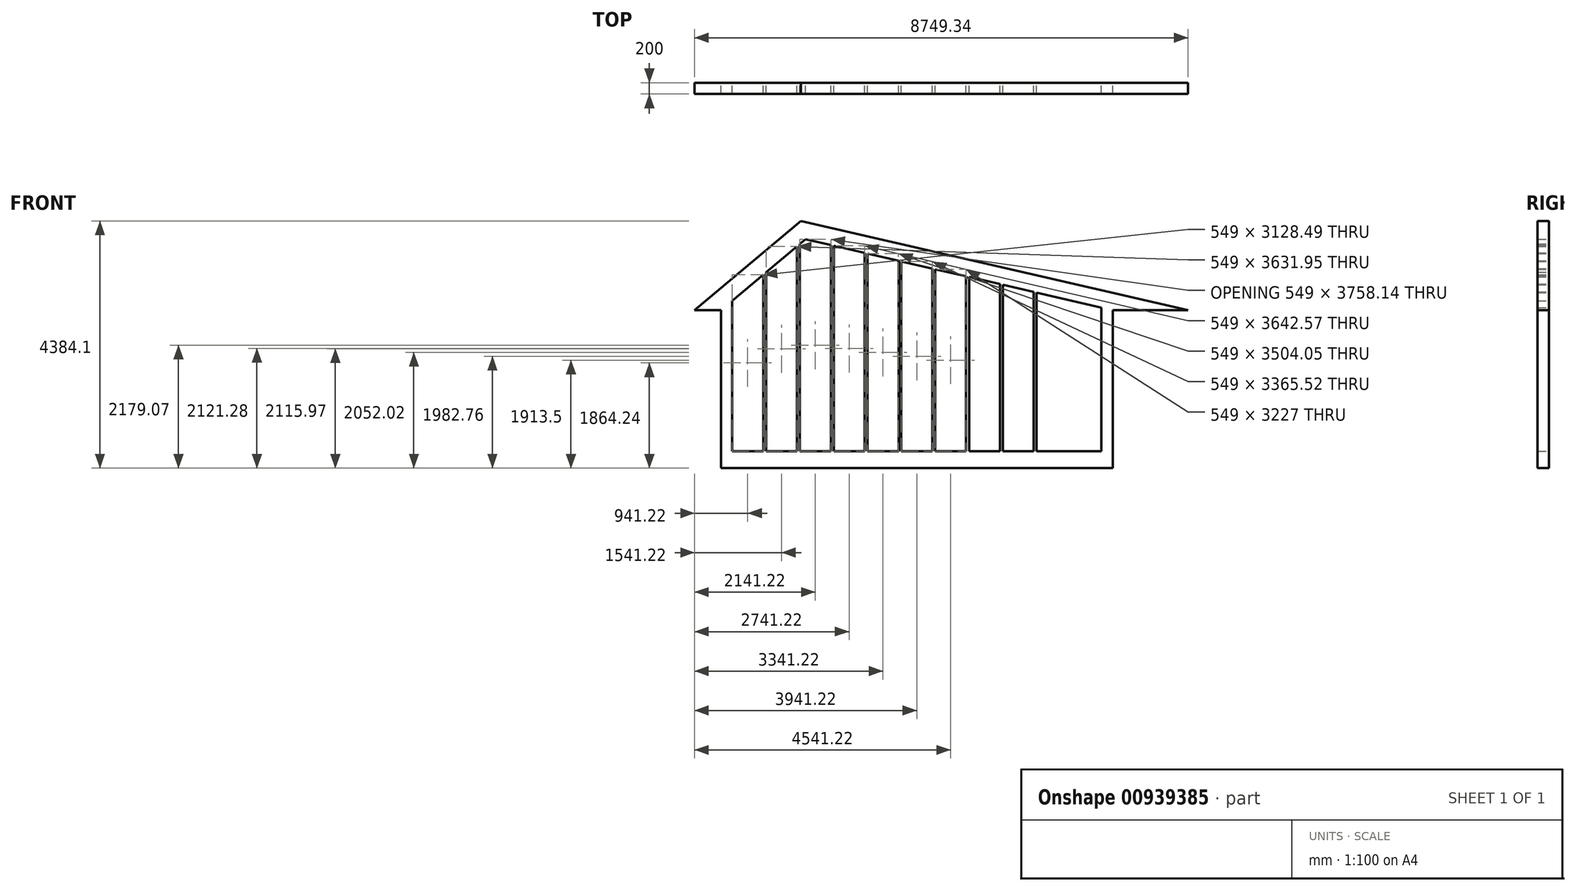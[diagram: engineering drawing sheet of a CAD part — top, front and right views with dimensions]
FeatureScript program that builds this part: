
annotation { "Feature Type Name" : "Feature", "Feature Type Description" : "" }
export const myFeature = defineFeature(function(context is Context, id is Id, definition is map)
    precondition{}
    {
        {
            var Q0;
            Q0=qCreatedBy(makeId("Front.planeOp"),FACE);
            var sketch = newSketch(context, id + "F0", { "sketchPlane" : qUnion([Q0])});
            skLineSegment(sketch, "E0", {"start": v(0, 0) * mm, "end": v(0, 2667.82) * mm});
            skLineSegment(sketch, "E1", {"start": v(0, 2667.82) * mm, "end": v(1299.4, 3758.14) * mm});
            skLineSegment(sketch, "E2", {"start": v(1299.4, 3758.14) * mm, "end": v(6549, 2546.17) * mm});
            skLineSegment(sketch, "E3", {"start": v(6549, 2546.17) * mm, "end": v(6549, 0) * mm});
            skLineSegment(sketch, "E4", {"start": v(6549, 0) * mm, "end": v(0, 0) * mm});
            skLineSegment(sketch, "E5", {"start": v(-200, -300) * mm, "end": v(-200, 2500) * mm});
            skLineSegment(sketch, "E6", {"start": v(-200, 2500) * mm, "end": v(-666.72, 2500) * mm});
            skLineSegment(sketch, "E7", {"start": v(-666.72, 2500) * mm, "end": v(1221.14, 4084.1) * mm});
            skLineSegment(sketch, "E8", {"start": v(1221.14, 4084.1) * mm, "end": v(8082.62, 2500) * mm});
            skLineSegment(sketch, "E9", {"start": v(8082.62, 2500) * mm, "end": v(6749, 2500) * mm});
            skLineSegment(sketch, "E10", {"start": v(6749, 2500) * mm, "end": v(6749, -300) * mm});
            skLineSegment(sketch, "E11", {"start": v(6749, -300) * mm, "end": v(-200, -300) * mm});
            skLineSegment(sketch, "E12", {"start": v(6549, 2546.17) * mm, "end": v(6749, 2500) * mm});
            skLineSegment(sketch, "E13", {"start": v(0, 2667.82) * mm, "end": v(-200, 2500) * mm});
            skLineSegment(sketch, "E14", {"start": v(6000, 0) * mm, "end": v(6000, 4084.1) * mm});
            skLineSegment(sketch, "E15", {"start": v(6000, 4084.1) * mm, "end": v(5949, 4084.1) * mm});
            skLineSegment(sketch, "E16", {"start": v(5949, 4084.1) * mm, "end": v(5949, 0) * mm});
            skLineSegment(sketch, "E17", {"start": v(5949, 0) * mm, "end": v(6000, 0) * mm});
            skLineSegment(sketch, "E18.1.0.0", {"start": v(5349, 4084.1) * mm, "end": v(5349, 0) * mm});
            skLineSegment(sketch, "E18.1.0.1", {"start": v(5400, 0) * mm, "end": v(5400, 4084.1) * mm});
            skLineSegment(sketch, "E18.2.0.0", {"start": v(4749, 4084.1) * mm, "end": v(4749, 0) * mm});
            skLineSegment(sketch, "E18.2.0.1", {"start": v(4800, 0) * mm, "end": v(4800, 4084.1) * mm});
            skLineSegment(sketch, "E18.3.0.0", {"start": v(4149, 4084.1) * mm, "end": v(4149, 0) * mm});
            skLineSegment(sketch, "E18.3.0.1", {"start": v(4200, 0) * mm, "end": v(4200, 4084.1) * mm});
            skLineSegment(sketch, "E18.4.0.0", {"start": v(3549, 4084.1) * mm, "end": v(3549, 0) * mm});
            skLineSegment(sketch, "E18.4.0.1", {"start": v(3600, 0) * mm, "end": v(3600, 4084.1) * mm});
            skLineSegment(sketch, "E18.5.0.0", {"start": v(2949, 4084.1) * mm, "end": v(2949, 0) * mm});
            skLineSegment(sketch, "E18.5.0.1", {"start": v(3000, 0) * mm, "end": v(3000, 4084.1) * mm});
            skLineSegment(sketch, "E18.6.0.0", {"start": v(2349, 4084.1) * mm, "end": v(2349, 0) * mm});
            skLineSegment(sketch, "E18.6.0.1", {"start": v(2400, 0) * mm, "end": v(2400, 4084.1) * mm});
            skLineSegment(sketch, "E18.7.0.0", {"start": v(1749, 4084.1) * mm, "end": v(1749, 0) * mm});
            skLineSegment(sketch, "E18.7.0.1", {"start": v(1800, 0) * mm, "end": v(1800, 4084.1) * mm});
            skLineSegment(sketch, "E18.8.0.0", {"start": v(1149, 4084.1) * mm, "end": v(1149, 0) * mm});
            skLineSegment(sketch, "E18.8.0.1", {"start": v(1200, 0) * mm, "end": v(1200, 4084.1) * mm});
            skLineSegment(sketch, "E18.9.0.0", {"start": v(549, 4084.1) * mm, "end": v(549, 0) * mm});
            skLineSegment(sketch, "E18.9.0.1", {"start": v(600, 0) * mm, "end": v(600, 4084.1) * mm});
            skLineSegment(sketch, "E18.direction1", {"start": v(6000, 0) * mm, "end": v(5400, 0) * mm, "construction": true});
            skSolve(sketch);
        }
        {
            var Q0;
            {var subQ1=sQuery(id+"F0.wireOp",EDGE,"E6");Q0=makeQuery(id+"F0.imprint","IMPRINT",FACE,{"disambiguationData":[TD([[makeQuery(id+"F0.imprint","IMPRINT",EDGE,{"derivedFrom":subQ1}),-1.0]])]});}
            var Q1;
            {var subQ0=sQuery(id+"F0.wireOp",EDGE,"E18.9.0.0");var subQ1=sQuery(id+"F0.wireOp",EDGE,"E1");var subQ2=makeQuery(id+"F0.imprint","INTERSECT",VERTEX,{"derivedFrom":[subQ1,subQ0]});Q1=makeQuery(id+"F0.imprint","IMPRINT",FACE,{"disambiguationData":[TD([[makeQuery(id+"F0.imprint","IMPRINT",EDGE,{"disambiguationData":[TD([[subQ2,-1.0]])],"derivedFrom":subQ1}),1.0]])]});}
            var Q2;
            {var subQ0=sQuery(id+"F0.wireOp",EDGE,"E18.9.0.1");var subQ1=sQuery(id+"F0.wireOp",EDGE,"E1");var subQ2=makeQuery(id+"F0.imprint","INTERSECT",VERTEX,{"derivedFrom":[subQ1,subQ0]});Q2=makeQuery(id+"F0.imprint","IMPRINT",FACE,{"disambiguationData":[TD([[makeQuery(id+"F0.imprint","IMPRINT",EDGE,{"disambiguationData":[TD([[subQ2,-1.0]])],"derivedFrom":subQ1}),1.0]])]});}
            var Q3;
            {var subQ0=sQuery(id+"F0.wireOp",EDGE,"E18.8.0.0");var subQ1=sQuery(id+"F0.wireOp",EDGE,"E1");var subQ2=makeQuery(id+"F0.imprint","INTERSECT",VERTEX,{"derivedFrom":[subQ1,subQ0]});Q3=makeQuery(id+"F0.imprint","IMPRINT",FACE,{"disambiguationData":[TD([[makeQuery(id+"F0.imprint","IMPRINT",EDGE,{"disambiguationData":[TD([[subQ2,-1.0]])],"derivedFrom":subQ1}),1.0]])]});}
            var Q4;
            {var subQ5=sQuery(id+"F0.wireOp",EDGE,"E2");var subQ6=sQuery(id+"F0.wireOp",EDGE,"E1");var subQ7=makeQuery(id+"F0.imprint","INTERSECT",VERTEX,{"derivedFrom":[subQ6,subQ5]});Q4=makeQuery(id+"F0.imprint","IMPRINT",FACE,{"disambiguationData":[TD([[makeQuery(id+"F0.imprint","IMPRINT",EDGE,{"disambiguationData":[TD([[subQ7,1.0]])],"derivedFrom":subQ6}),1.0]])]});}
            var Q5;
            {var subQ0=sQuery(id+"F0.wireOp",EDGE,"E18.7.0.0");var subQ1=sQuery(id+"F0.wireOp",EDGE,"E2");var subQ2=makeQuery(id+"F0.imprint","INTERSECT",VERTEX,{"derivedFrom":[subQ1,subQ0]});Q5=makeQuery(id+"F0.imprint","IMPRINT",FACE,{"disambiguationData":[TD([[makeQuery(id+"F0.imprint","IMPRINT",EDGE,{"disambiguationData":[TD([[subQ2,-1.0]])],"derivedFrom":subQ1}),1.0]])]});}
            var Q6;
            {var subQ0=sQuery(id+"F0.wireOp",EDGE,"E18.7.0.1");var subQ1=sQuery(id+"F0.wireOp",EDGE,"E2");var subQ2=makeQuery(id+"F0.imprint","INTERSECT",VERTEX,{"derivedFrom":[subQ1,subQ0]});Q6=makeQuery(id+"F0.imprint","IMPRINT",FACE,{"disambiguationData":[TD([[makeQuery(id+"F0.imprint","IMPRINT",EDGE,{"disambiguationData":[TD([[subQ2,-1.0]])],"derivedFrom":subQ1}),1.0]])]});}
            var Q7;
            {var subQ0=sQuery(id+"F0.wireOp",EDGE,"E18.6.0.0");var subQ1=sQuery(id+"F0.wireOp",EDGE,"E2");var subQ2=makeQuery(id+"F0.imprint","INTERSECT",VERTEX,{"derivedFrom":[subQ1,subQ0]});Q7=makeQuery(id+"F0.imprint","IMPRINT",FACE,{"disambiguationData":[TD([[makeQuery(id+"F0.imprint","IMPRINT",EDGE,{"disambiguationData":[TD([[subQ2,-1.0]])],"derivedFrom":subQ1}),1.0]])]});}
            var Q8;
            {var subQ0=sQuery(id+"F0.wireOp",EDGE,"E18.6.0.1");var subQ1=sQuery(id+"F0.wireOp",EDGE,"E2");var subQ2=makeQuery(id+"F0.imprint","INTERSECT",VERTEX,{"derivedFrom":[subQ1,subQ0]});Q8=makeQuery(id+"F0.imprint","IMPRINT",FACE,{"disambiguationData":[TD([[makeQuery(id+"F0.imprint","IMPRINT",EDGE,{"disambiguationData":[TD([[subQ2,-1.0]])],"derivedFrom":subQ1}),1.0]])]});}
            var Q9;
            {var subQ0=sQuery(id+"F0.wireOp",EDGE,"E18.5.0.0");var subQ1=sQuery(id+"F0.wireOp",EDGE,"E2");var subQ2=makeQuery(id+"F0.imprint","INTERSECT",VERTEX,{"derivedFrom":[subQ1,subQ0]});Q9=makeQuery(id+"F0.imprint","IMPRINT",FACE,{"disambiguationData":[TD([[makeQuery(id+"F0.imprint","IMPRINT",EDGE,{"disambiguationData":[TD([[subQ2,-1.0]])],"derivedFrom":subQ1}),1.0]])]});}
            var Q10;
            {var subQ0=sQuery(id+"F0.wireOp",EDGE,"E18.5.0.1");var subQ1=sQuery(id+"F0.wireOp",EDGE,"E2");var subQ2=makeQuery(id+"F0.imprint","INTERSECT",VERTEX,{"derivedFrom":[subQ1,subQ0]});Q10=makeQuery(id+"F0.imprint","IMPRINT",FACE,{"disambiguationData":[TD([[makeQuery(id+"F0.imprint","IMPRINT",EDGE,{"disambiguationData":[TD([[subQ2,-1.0]])],"derivedFrom":subQ1}),1.0]])]});}
            var Q11;
            {var subQ0=sQuery(id+"F0.wireOp",EDGE,"E18.4.0.0");var subQ1=sQuery(id+"F0.wireOp",EDGE,"E2");var subQ2=makeQuery(id+"F0.imprint","INTERSECT",VERTEX,{"derivedFrom":[subQ1,subQ0]});Q11=makeQuery(id+"F0.imprint","IMPRINT",FACE,{"disambiguationData":[TD([[makeQuery(id+"F0.imprint","IMPRINT",EDGE,{"disambiguationData":[TD([[subQ2,-1.0]])],"derivedFrom":subQ1}),1.0]])]});}
            var Q12;
            {var subQ0=sQuery(id+"F0.wireOp",EDGE,"E18.4.0.1");var subQ1=sQuery(id+"F0.wireOp",EDGE,"E2");var subQ2=makeQuery(id+"F0.imprint","INTERSECT",VERTEX,{"derivedFrom":[subQ1,subQ0]});Q12=makeQuery(id+"F0.imprint","IMPRINT",FACE,{"disambiguationData":[TD([[makeQuery(id+"F0.imprint","IMPRINT",EDGE,{"disambiguationData":[TD([[subQ2,-1.0]])],"derivedFrom":subQ1}),1.0]])]});}
            var Q13;
            {var subQ0=sQuery(id+"F0.wireOp",EDGE,"E18.3.0.0");var subQ1=sQuery(id+"F0.wireOp",EDGE,"E2");var subQ2=makeQuery(id+"F0.imprint","INTERSECT",VERTEX,{"derivedFrom":[subQ1,subQ0]});Q13=makeQuery(id+"F0.imprint","IMPRINT",FACE,{"disambiguationData":[TD([[makeQuery(id+"F0.imprint","IMPRINT",EDGE,{"disambiguationData":[TD([[subQ2,-1.0]])],"derivedFrom":subQ1}),1.0]])]});}
            var Q14;
            {var subQ0=sQuery(id+"F0.wireOp",EDGE,"E18.3.0.1");var subQ1=sQuery(id+"F0.wireOp",EDGE,"E2");var subQ2=makeQuery(id+"F0.imprint","INTERSECT",VERTEX,{"derivedFrom":[subQ1,subQ0]});Q14=makeQuery(id+"F0.imprint","IMPRINT",FACE,{"disambiguationData":[TD([[makeQuery(id+"F0.imprint","IMPRINT",EDGE,{"disambiguationData":[TD([[subQ2,-1.0]])],"derivedFrom":subQ1}),1.0]])]});}
            var Q15;
            {var subQ0=sQuery(id+"F0.wireOp",EDGE,"E18.2.0.0");var subQ1=sQuery(id+"F0.wireOp",EDGE,"E2");var subQ2=makeQuery(id+"F0.imprint","INTERSECT",VERTEX,{"derivedFrom":[subQ1,subQ0]});Q15=makeQuery(id+"F0.imprint","IMPRINT",FACE,{"disambiguationData":[TD([[makeQuery(id+"F0.imprint","IMPRINT",EDGE,{"disambiguationData":[TD([[subQ2,-1.0]])],"derivedFrom":subQ1}),1.0]])]});}
            var Q16;
            {var subQ0=sQuery(id+"F0.wireOp",EDGE,"E18.2.0.1");var subQ1=sQuery(id+"F0.wireOp",EDGE,"E2");var subQ2=makeQuery(id+"F0.imprint","INTERSECT",VERTEX,{"derivedFrom":[subQ1,subQ0]});Q16=makeQuery(id+"F0.imprint","IMPRINT",FACE,{"disambiguationData":[TD([[makeQuery(id+"F0.imprint","IMPRINT",EDGE,{"disambiguationData":[TD([[subQ2,-1.0]])],"derivedFrom":subQ1}),1.0]])]});}
            var Q17;
            {var subQ0=sQuery(id+"F0.wireOp",EDGE,"E18.1.0.0");var subQ1=sQuery(id+"F0.wireOp",EDGE,"E2");var subQ2=makeQuery(id+"F0.imprint","INTERSECT",VERTEX,{"derivedFrom":[subQ1,subQ0]});Q17=makeQuery(id+"F0.imprint","IMPRINT",FACE,{"disambiguationData":[TD([[makeQuery(id+"F0.imprint","IMPRINT",EDGE,{"disambiguationData":[TD([[subQ2,-1.0]])],"derivedFrom":subQ1}),1.0]])]});}
            var Q18;
            {var subQ0=sQuery(id+"F0.wireOp",EDGE,"E18.1.0.1");var subQ1=sQuery(id+"F0.wireOp",EDGE,"E2");var subQ2=makeQuery(id+"F0.imprint","INTERSECT",VERTEX,{"derivedFrom":[subQ1,subQ0]});Q18=makeQuery(id+"F0.imprint","IMPRINT",FACE,{"disambiguationData":[TD([[makeQuery(id+"F0.imprint","IMPRINT",EDGE,{"disambiguationData":[TD([[subQ2,-1.0]])],"derivedFrom":subQ1}),1.0]])]});}
            var Q19;
            {var subQ1=sQuery(id+"F0.wireOp",EDGE,"E9");Q19=makeQuery(id+"F0.imprint","IMPRINT",FACE,{"disambiguationData":[TD([[makeQuery(id+"F0.imprint","IMPRINT",EDGE,{"derivedFrom":subQ1}),-1.0]])]});}
            var Q20;
            {var subQ0=sQuery(id+"F0.wireOp",EDGE,"E16");var subQ1=sQuery(id+"F0.wireOp",EDGE,"E2");var subQ2=makeQuery(id+"F0.imprint","INTERSECT",VERTEX,{"derivedFrom":[subQ1,subQ0]});Q20=makeQuery(id+"F0.imprint","IMPRINT",FACE,{"disambiguationData":[TD([[makeQuery(id+"F0.imprint","IMPRINT",EDGE,{"disambiguationData":[TD([[subQ2,-1.0]])],"derivedFrom":subQ1}),1.0]])]});}
            var Q21;
            {var subQ1=sQuery(id+"F0.wireOp",EDGE,"E0");Q21=makeQuery(id+"F0.imprint","IMPRINT",FACE,{"disambiguationData":[TD([[makeQuery(id+"F0.imprint","IMPRINT",EDGE,{"derivedFrom":subQ1}),1.0]])]});}
            var Q22;
            {var subQ5=sQuery(id+"F0.wireOp",EDGE,"E17");Q22=makeQuery(id+"F0.imprint","IMPRINT",FACE,{"disambiguationData":[TD([[makeQuery(id+"F0.imprint","IMPRINT",EDGE,{"derivedFrom":subQ5}),1.0]])]});}
            var Q23;
            {var subQ0=sQuery(id+"F0.wireOp",EDGE,"E18.1.0.0");var subQ1=sQuery(id+"F0.wireOp",EDGE,"E2");var subQ2=makeQuery(id+"F0.imprint","INTERSECT",VERTEX,{"derivedFrom":[subQ1,subQ0]});Q23=makeQuery(id+"F0.imprint","IMPRINT",FACE,{"disambiguationData":[TD([[makeQuery(id+"F0.imprint","IMPRINT",EDGE,{"disambiguationData":[TD([[subQ2,-1.0]])],"derivedFrom":subQ1}),-1.0]])]});}
            var Q24;
            {var subQ0=sQuery(id+"F0.wireOp",EDGE,"E18.2.0.0");var subQ1=sQuery(id+"F0.wireOp",EDGE,"E2");var subQ2=makeQuery(id+"F0.imprint","INTERSECT",VERTEX,{"derivedFrom":[subQ1,subQ0]});Q24=makeQuery(id+"F0.imprint","IMPRINT",FACE,{"disambiguationData":[TD([[makeQuery(id+"F0.imprint","IMPRINT",EDGE,{"disambiguationData":[TD([[subQ2,-1.0]])],"derivedFrom":subQ1}),-1.0]])]});}
            var Q25;
            {var subQ0=sQuery(id+"F0.wireOp",EDGE,"E18.3.0.0");var subQ1=sQuery(id+"F0.wireOp",EDGE,"E2");var subQ2=makeQuery(id+"F0.imprint","INTERSECT",VERTEX,{"derivedFrom":[subQ1,subQ0]});Q25=makeQuery(id+"F0.imprint","IMPRINT",FACE,{"disambiguationData":[TD([[makeQuery(id+"F0.imprint","IMPRINT",EDGE,{"disambiguationData":[TD([[subQ2,-1.0]])],"derivedFrom":subQ1}),-1.0]])]});}
            var Q26;
            {var subQ0=sQuery(id+"F0.wireOp",EDGE,"E18.4.0.0");var subQ1=sQuery(id+"F0.wireOp",EDGE,"E2");var subQ2=makeQuery(id+"F0.imprint","INTERSECT",VERTEX,{"derivedFrom":[subQ1,subQ0]});Q26=makeQuery(id+"F0.imprint","IMPRINT",FACE,{"disambiguationData":[TD([[makeQuery(id+"F0.imprint","IMPRINT",EDGE,{"disambiguationData":[TD([[subQ2,-1.0]])],"derivedFrom":subQ1}),-1.0]])]});}
            var Q27;
            {var subQ0=sQuery(id+"F0.wireOp",EDGE,"E18.5.0.0");var subQ1=sQuery(id+"F0.wireOp",EDGE,"E2");var subQ2=makeQuery(id+"F0.imprint","INTERSECT",VERTEX,{"derivedFrom":[subQ1,subQ0]});Q27=makeQuery(id+"F0.imprint","IMPRINT",FACE,{"disambiguationData":[TD([[makeQuery(id+"F0.imprint","IMPRINT",EDGE,{"disambiguationData":[TD([[subQ2,-1.0]])],"derivedFrom":subQ1}),-1.0]])]});}
            var Q28;
            {var subQ0=sQuery(id+"F0.wireOp",EDGE,"E18.6.0.0");var subQ1=sQuery(id+"F0.wireOp",EDGE,"E2");var subQ2=makeQuery(id+"F0.imprint","INTERSECT",VERTEX,{"derivedFrom":[subQ1,subQ0]});Q28=makeQuery(id+"F0.imprint","IMPRINT",FACE,{"disambiguationData":[TD([[makeQuery(id+"F0.imprint","IMPRINT",EDGE,{"disambiguationData":[TD([[subQ2,-1.0]])],"derivedFrom":subQ1}),-1.0]])]});}
            var Q29;
            {var subQ0=sQuery(id+"F0.wireOp",EDGE,"E18.7.0.0");var subQ1=sQuery(id+"F0.wireOp",EDGE,"E2");var subQ2=makeQuery(id+"F0.imprint","INTERSECT",VERTEX,{"derivedFrom":[subQ1,subQ0]});Q29=makeQuery(id+"F0.imprint","IMPRINT",FACE,{"disambiguationData":[TD([[makeQuery(id+"F0.imprint","IMPRINT",EDGE,{"disambiguationData":[TD([[subQ2,-1.0]])],"derivedFrom":subQ1}),-1.0]])]});}
            var Q30;
            {var subQ0=sQuery(id+"F0.wireOp",EDGE,"E18.8.0.0");var subQ1=sQuery(id+"F0.wireOp",EDGE,"E1");var subQ2=makeQuery(id+"F0.imprint","INTERSECT",VERTEX,{"derivedFrom":[subQ1,subQ0]});Q30=makeQuery(id+"F0.imprint","IMPRINT",FACE,{"disambiguationData":[TD([[makeQuery(id+"F0.imprint","IMPRINT",EDGE,{"disambiguationData":[TD([[subQ2,-1.0]])],"derivedFrom":subQ1}),-1.0]])]});}
            var Q31;
            {var subQ0=sQuery(id+"F0.wireOp",EDGE,"E18.9.0.0");var subQ1=sQuery(id+"F0.wireOp",EDGE,"E1");var subQ2=makeQuery(id+"F0.imprint","INTERSECT",VERTEX,{"derivedFrom":[subQ1,subQ0]});Q31=makeQuery(id+"F0.imprint","IMPRINT",FACE,{"disambiguationData":[TD([[makeQuery(id+"F0.imprint","IMPRINT",EDGE,{"disambiguationData":[TD([[subQ2,-1.0]])],"derivedFrom":subQ1}),-1.0]])]});}
            extrude(context, id + "F1", {"entities" : qUnion([Q0, Q1, Q2, Q3, Q4, Q5, Q6, Q7, Q8, Q9, Q10, Q11, Q12, Q13, Q14, Q15, Q16, Q17, Q18, Q19, Q20, Q21, Q22, Q23, Q24, Q25, Q26, Q27, Q28, Q29, Q30, Q31]), "depth" : 200 * mm, "offsetDistance" : 25 * mm});
        }
    });
